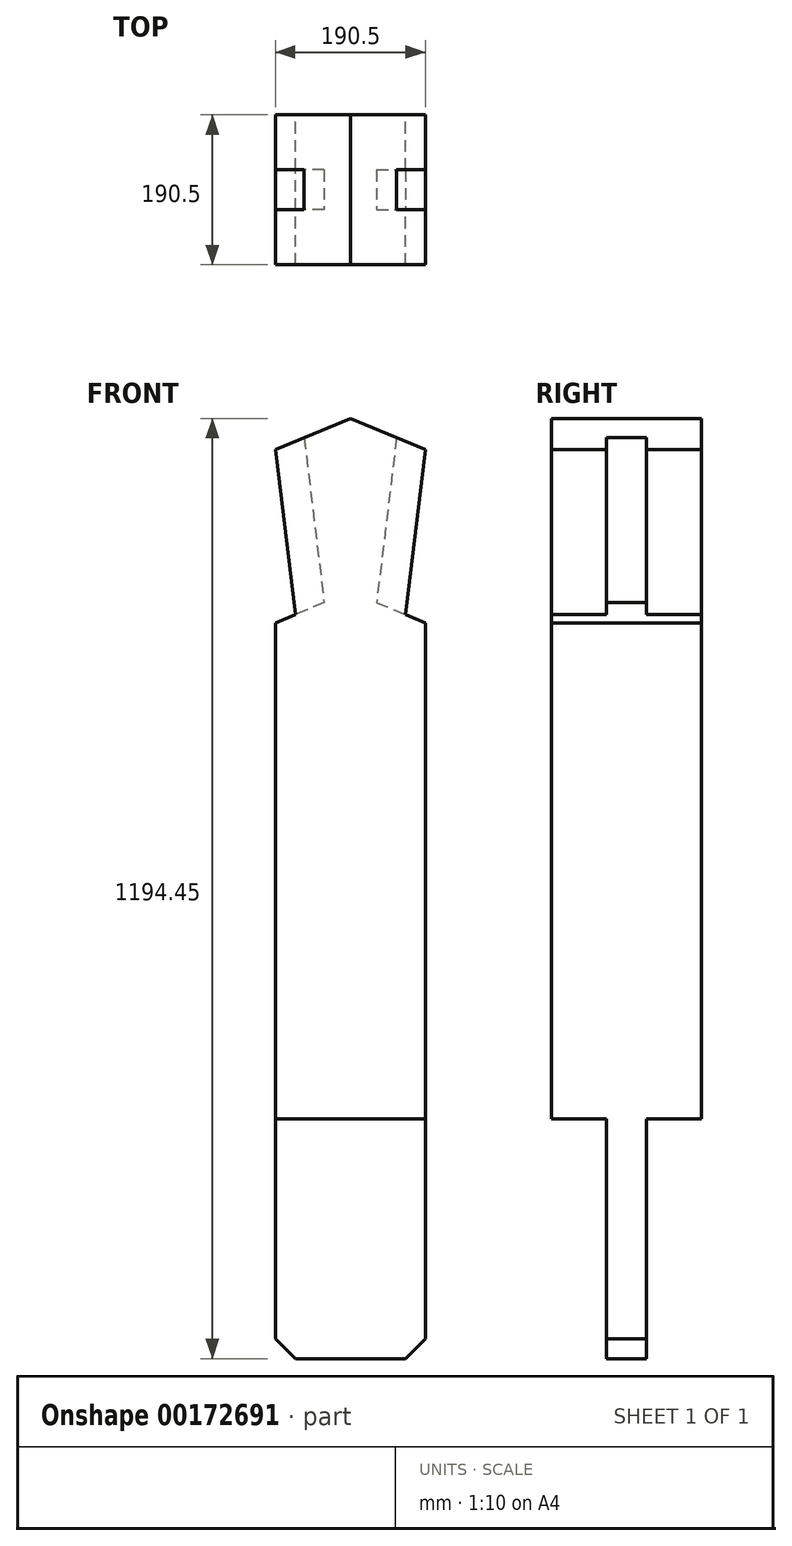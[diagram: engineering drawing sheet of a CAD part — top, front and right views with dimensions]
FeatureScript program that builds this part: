
annotation { "Feature Type Name" : "Feature", "Feature Type Description" : "" }
export const myFeature = defineFeature(function(context is Context, id is Id, definition is map)
    precondition{}
    {
        {
            var Q0;
            Q0=qCreatedBy(makeId("Front.planeOp"),FACE);
            var sketch = newSketch(context, id + "F0", { "sketchPlane" : qUnion([Q0])});
            skLineSegment(sketch, "E0.bottom", {"start": v(-95.25, 1092.85) * mm, "end": v(95.25, 1092.85) * mm});
            skLineSegment(sketch, "E0.top", {"start": v(-95.25, -101.6) * mm, "end": v(95.25, -101.6) * mm});
            skLineSegment(sketch, "E0.left", {"start": v(-95.25, 833.03) * mm, "end": v(-95.25, 203.2) * mm});
            skLineSegment(sketch, "E0.right", {"start": v(95.25, 833.03) * mm, "end": v(95.25, 203.2) * mm});
            skLineSegment(sketch, "E1", {"start": v(-95.25, 0) * mm, "end": v(95.25, 0) * mm});
            skLineSegment(sketch, "E2", {"start": v(95.25, 0) * mm, "end": v(2094.52, 0) * mm});
            skLineSegment(sketch, "E3", {"start": v(2094.52, 0) * mm, "end": v(1606.84, 203.2) * mm});
            skLineSegment(sketch, "E4", {"start": v(1606.84, 203.2) * mm, "end": v(95.25, 203.2) * mm});
            skLineSegment(sketch, "E5", {"start": v(95.25, 203.2) * mm, "end": v(-95.25, 203.2) * mm});
            skLineSegment(sketch, "E6", {"start": v(-95.25, 203.2) * mm, "end": v(-1606.84, 203.2) * mm});
            skLineSegment(sketch, "E7", {"start": v(-1606.84, 203.2) * mm, "end": v(-2094.52, 0) * mm});
            skLineSegment(sketch, "E8", {"start": v(-2094.52, 0) * mm, "end": v(-95.25, 0) * mm});
            skLineSegment(sketch, "E9", {"start": v(1850.68, 101.6) * mm, "end": v(1820.2, 101.6) * mm});
            skLineSegment(sketch, "E10", {"start": v(1820.2, 101.6) * mm, "end": v(1820.2, 114.3) * mm});
            skLineSegment(sketch, "E11", {"start": v(1606.84, 203.2) * mm, "end": v(95.25, 833.03) * mm});
            skLineSegment(sketch, "E12", {"start": v(33.32, 858.84) * mm, "end": v(0, 872.72) * mm});
            skLineSegment(sketch, "E13", {"start": v(0, 872.72) * mm, "end": v(0, 1092.85) * mm});
            skLineSegment(sketch, "E14", {"start": v(0, 1092.85) * mm, "end": v(69.85, 1063.75) * mm});
            skLineSegment(sketch, "E15", {"start": v(95.25, 1053.16) * mm, "end": v(3048, -177.15) * mm});
            skLineSegment(sketch, "E16", {"start": v(3048, -177.15) * mm, "end": v(3048, -397.28) * mm});
            skLineSegment(sketch, "E17", {"start": v(3048, -397.28) * mm, "end": v(2094.52, 0) * mm});
            skLineSegment(sketch, "E18", {"start": v(1014.13, 450.16) * mm, "end": v(1092.29, 637.73) * mm});
            skLineSegment(sketch, "E19", {"start": v(2235.2, -58.62) * mm, "end": v(2235.2, -2361.55) * mm});
            skLineSegment(sketch, "E20", {"start": v(2235.2, -2361.55) * mm, "end": v(2438.4, -2361.55) * mm});
            skLineSegment(sketch, "E21", {"start": v(2438.4, -2361.55) * mm, "end": v(2438.4, -143.28) * mm});
            skLineSegment(sketch, "E22", {"start": v(0, 0) * mm, "end": v(0, -1827.58) * mm});
            skLineSegment(sketch, "E23", {"start": v(2438.4, -143.28) * mm, "end": v(2438.4, 76.85) * mm});
            skLineSegment(sketch, "E24", {"start": v(69.85, 1063.75) * mm, "end": v(69.85, 843.61) * mm});
            skLineSegment(sketch, "E25", {"start": v(95.25, 1053.16) * mm, "end": v(69.85, 843.61) * mm});
            skLineSegment(sketch, "E26.0", {"start": v(58.72, 1068.39) * mm, "end": v(33.32, 858.84) * mm});
            skLineSegment(sketch, "E27.MirrorCS", {"start": v(0, 1092.85) * mm, "end": v(-69.85, 1063.75) * mm});
            skLineSegment(sketch, "E28.MirrorCS", {"start": v(-33.32, 858.84) * mm, "end": v(0, 872.72) * mm});
            skLineSegment(sketch, "E29.MirrorCS", {"start": v(-95.25, 1053.16) * mm, "end": v(-69.85, 843.61) * mm});
            skLineSegment(sketch, "E30.MirrorCS", {"start": v(-1014.13, 450.16) * mm, "end": v(-1092.29, 637.73) * mm});
            skLineSegment(sketch, "E31.MirrorCS", {"start": v(-69.85, 1063.75) * mm, "end": v(-69.85, 843.61) * mm});
            skLineSegment(sketch, "E32.MirrorCS", {"start": v(-58.72, 1068.39) * mm, "end": v(-33.32, 858.84) * mm});
            skLineSegment(sketch, "E33.MirrorCS", {"start": v(-95.25, 1053.16) * mm, "end": v(-3048, -177.15) * mm});
            skLineSegment(sketch, "E34.MirrorCS", {"start": v(-1606.84, 203.2) * mm, "end": v(-95.25, 833.03) * mm});
            skLineSegment(sketch, "E35.MirrorCS", {"start": v(-3048, -177.15) * mm, "end": v(-3048, -397.28) * mm});
            skLineSegment(sketch, "E36.MirrorCS", {"start": v(-3048, -397.28) * mm, "end": v(-2094.52, 0) * mm});
            skLineSegment(sketch, "E37.MirrorCS", {"start": v(-2235.2, -58.62) * mm, "end": v(-2235.2, -2361.55) * mm});
            skLineSegment(sketch, "E38.MirrorCS", {"start": v(-2235.2, -2361.55) * mm, "end": v(-2438.4, -2361.55) * mm});
            skLineSegment(sketch, "E39.MirrorCS", {"start": v(-2438.4, -2361.55) * mm, "end": v(-2438.4, -143.28) * mm});
            skLineSegment(sketch, "E40", {"start": v(95.25, 833.03) * mm, "end": v(95.25, 1053.16) * mm});
            skLineSegment(sketch, "E41", {"start": v(95.25, 1092.85) * mm, "end": v(95.25, 1053.16) * mm});
            skLineSegment(sketch, "E42", {"start": v(-95.25, 833.03) * mm, "end": v(-95.25, 1053.16) * mm});
            skLineSegment(sketch, "E43", {"start": v(-95.25, 1092.85) * mm, "end": v(-95.25, 1053.16) * mm});
            skLineSegment(sketch, "E44", {"start": v(33.32, 858.84) * mm, "end": v(69.85, 843.61) * mm});
            skLineSegment(sketch, "E45", {"start": v(95.25, 833.03) * mm, "end": v(69.85, 843.61) * mm});
            skLineSegment(sketch, "E46", {"start": v(-33.32, 858.84) * mm, "end": v(-69.85, 843.61) * mm});
            skLineSegment(sketch, "E47", {"start": v(-95.25, 833.03) * mm, "end": v(-69.85, 843.61) * mm});
            skLineSegment(sketch, "E48", {"start": v(-95.25, 1053.16) * mm, "end": v(-58.72, 1068.39) * mm});
            skLineSegment(sketch, "E49", {"start": v(58.72, 1068.39) * mm, "end": v(69.85, 1063.75) * mm});
            skLineSegment(sketch, "E50", {"start": v(58.72, 1068.39) * mm, "end": v(95.25, 1053.16) * mm});
            skLineSegment(sketch, "E51", {"start": v(-69.85, 1063.75) * mm, "end": v(-58.72, 1068.39) * mm});
            skLineSegment(sketch, "E52", {"start": v(-95.25, 203.2) * mm, "end": v(-95.25, 0) * mm});
            skLineSegment(sketch, "E53", {"start": v(-95.25, 0) * mm, "end": v(-95.25, -101.6) * mm});
            skLineSegment(sketch, "E54", {"start": v(95.25, 203.2) * mm, "end": v(95.25, 0) * mm});
            skLineSegment(sketch, "E55", {"start": v(95.25, 0) * mm, "end": v(95.25, -101.6) * mm});
            skSolve(sketch);
        }
        {
            var Q0;
            {var subQ0=sQuery(id+"F0.wireOp",EDGE,"E55");Q0=makeQuery(id+"F0.imprint","IMPRINT",FACE,{"disambiguationData":[TD([[makeQuery(id+"F0.imprint","IMPRINT",EDGE,{"derivedFrom":subQ0}),-1.0]])]});}
            var Q1;
            {var subQ0=sQuery(id+"F0.wireOp",EDGE,"E53");Q1=makeQuery(id+"F0.imprint","IMPRINT",FACE,{"disambiguationData":[TD([[makeQuery(id+"F0.imprint","IMPRINT",EDGE,{"derivedFrom":subQ0}),1.0]])]});}
            var Q2;
            Q2=makeQuery(id+"F0.imprint","IMPRINT",FACE,{"disambiguationData":[TD([[makeQuery(id+"F0.imprint","IMPRINT",EDGE,{"derivedFrom":sQuery(id+"F0.wireOp",EDGE,"E5")}),1.0]])]});
            var Q3;
            Q3=makeQuery(id+"F0.imprint","IMPRINT",FACE,{"disambiguationData":[TD([[makeQuery(id+"F0.imprint","IMPRINT",EDGE,{"derivedFrom":sQuery(id+"F0.wireOp",EDGE,"E0.left")}),1.0]])]});
            var Q4;
            Q4=makeQuery(id+"F0.imprint","IMPRINT",FACE,{"disambiguationData":[TD([[makeQuery(id+"F0.imprint","IMPRINT",EDGE,{"derivedFrom":sQuery(id+"F0.wireOp",EDGE,"E13")}),1.0]])]});
            var Q5;
            {var subQ4=sQuery(id+"F0.wireOp",EDGE,"E12");Q5=makeQuery(id+"F0.imprint","IMPRINT",FACE,{"disambiguationData":[TD([[makeQuery(id+"F0.imprint","IMPRINT",EDGE,{"derivedFrom":subQ4}),-1.0]])]});}
            var Q6;
            {var subQ0=sQuery(id+"F0.wireOp",EDGE,"E51");Q6=makeQuery(id+"F0.imprint","IMPRINT",FACE,{"disambiguationData":[TD([[makeQuery(id+"F0.imprint","IMPRINT",EDGE,{"derivedFrom":subQ0}),-1.0]])]});}
            var Q7;
            {var subQ0=sQuery(id+"F0.wireOp",EDGE,"E49");Q7=makeQuery(id+"F0.imprint","IMPRINT",FACE,{"disambiguationData":[TD([[makeQuery(id+"F0.imprint","IMPRINT",EDGE,{"derivedFrom":subQ0}),-1.0]])]});}
            var Q8;
            {var subQ0=sQuery(id+"F0.wireOp",EDGE,"E46");Q8=makeQuery(id+"F0.imprint","IMPRINT",FACE,{"disambiguationData":[TD([[makeQuery(id+"F0.imprint","IMPRINT",EDGE,{"derivedFrom":subQ0}),-1.0]])]});}
            var Q9;
            {var subQ0=sQuery(id+"F0.wireOp",EDGE,"E29.MirrorCS");Q9=makeQuery(id+"F0.imprint","IMPRINT",FACE,{"disambiguationData":[TD([[makeQuery(id+"F0.imprint","IMPRINT",EDGE,{"derivedFrom":subQ0}),1.0]])]});}
            var Q10;
            {var subQ0=sQuery(id+"F0.wireOp",EDGE,"E25");Q10=makeQuery(id+"F0.imprint","IMPRINT",FACE,{"disambiguationData":[TD([[makeQuery(id+"F0.imprint","IMPRINT",EDGE,{"derivedFrom":subQ0}),-1.0]])]});}
            var Q11;
            {var subQ0=sQuery(id+"F0.wireOp",EDGE,"E44");Q11=makeQuery(id+"F0.imprint","IMPRINT",FACE,{"disambiguationData":[TD([[makeQuery(id+"F0.imprint","IMPRINT",EDGE,{"derivedFrom":subQ0}),1.0]])]});}
            extrude(context, id + "F1", {"entities" : qUnion([Q0, Q1, Q2, Q3, Q4, Q5, Q6, Q7, Q8, Q9, Q10, Q11]), "endBound" : BoundingType.SYMMETRIC, "depth" : 190.5 * mm});
        }
        {
            var Q0;
            Q0=qCreatedBy(makeId("Right.planeOp"),FACE);
            var sketch = newSketch(context, id + "F2", { "sketchPlane" : qUnion([Q0])});
            skLineSegment(sketch, "E56.bottom", {"start": v(-95.25, -101.6) * mm, "end": v(-25.4, -101.6) * mm});
            skLineSegment(sketch, "E56.top", {"start": v(-95.25, 203.2) * mm, "end": v(-25.4, 203.2) * mm});
            skLineSegment(sketch, "E56.left", {"start": v(-95.25, -101.6) * mm, "end": v(-95.25, 203.2) * mm});
            skLineSegment(sketch, "E56.right", {"start": v(-25.4, -101.6) * mm, "end": v(-25.4, 203.2) * mm});
            skLineSegment(sketch, "E57.bottom", {"start": v(95.25, -101.6) * mm, "end": v(25.4, -101.6) * mm});
            skLineSegment(sketch, "E57.top", {"start": v(95.25, 203.2) * mm, "end": v(25.4, 203.2) * mm});
            skLineSegment(sketch, "E57.left", {"start": v(95.25, -101.6) * mm, "end": v(95.25, 203.2) * mm});
            skLineSegment(sketch, "E57.right", {"start": v(25.4, -101.6) * mm, "end": v(25.4, 203.2) * mm});
            skSolve(sketch);
        }
        {
            var Q0;
            Q0 = qSketchRegion(id + "F2", true);
            extrude(context, id + "F3", {"entities" : qUnion([Q0]), "operationType" : NewBodyOperationType.REMOVE, "endBound" : BoundingType.THROUGH_ALL, "oppositeDirection" : true, "depth" : 25.4 * mm, "hasSecondDirection" : true, "secondDirectionBound" : SecondDirectionBoundingType.THROUGH_ALL, "secondDirectionOppositeDirection" : false, "secondDirectionDepth" : 25.4 * mm});
        }
        {
            var Q0;
            Q0=makeQuery(id+"F1.opExtrude","SWEPT_FACE",FACE,{"disambiguationData":[OSD([sQuery(id+"F0.wireOp",EDGE,"E14"),sQuery(id+"F0.wireOp",EDGE,"E49"),sQuery(id+"F0.wireOp",EDGE,"E50")])]});
            var sketch = newSketch(context, id + "F4", { "sketchPlane" : qUnion([Q0])});
            skLineSegment(sketch, "E58.bottom", {"start": v(-356.72, 25.4) * mm, "end": v(-317.14, 25.4) * mm});
            skLineSegment(sketch, "E58.top", {"start": v(-356.72, -25.4) * mm, "end": v(-317.14, -25.4) * mm});
            skLineSegment(sketch, "E58.left", {"start": v(-356.72, 25.4) * mm, "end": v(-356.72, -25.4) * mm});
            skLineSegment(sketch, "E58.right", {"start": v(-317.14, 25.4) * mm, "end": v(-317.14, -25.4) * mm});
            skSolve(sketch);
        }
        {
            var Q0;
            Q0=makeQuery(id+"F1.opExtrude","SWEPT_EDGE",EDGE,{"disambiguationData":[OSD([sQuery(id+"F0.wireOp",EDGE,"E0.top"),sQuery(id+"F0.wireOp",EDGE,"E55")])]});
            chamfer(context, id + "F5", {"entities" : qUnion([Q0]), "width" : 25.4 * mm, "tangentPropagation" : true});
        }
        {
            var Q0;
            Q0=makeQuery(id+"F1.opExtrude","SWEPT_EDGE",EDGE,{"disambiguationData":[OSD([sQuery(id+"F0.wireOp",EDGE,"E0.top"),sQuery(id+"F0.wireOp",EDGE,"E53")])]});
            chamfer(context, id + "F6", {"entities" : qUnion([Q0]), "width" : 25.4 * mm, "tangentPropagation" : true});
        }
        {
            var Q0;
            Q0=qCreatedBy(makeId("Front.planeOp"),FACE);
            var sketch = newSketch(context, id + "F7", { "sketchPlane" : qUnion([Q0])});
            skLineSegment(sketch, "E59", {"start": v(33.32, 858.84) * mm, "end": v(69.85, 843.61) * mm});
            skLineSegment(sketch, "E60", {"start": v(69.85, 843.61) * mm, "end": v(95.25, 1053.16) * mm});
            skLineSegment(sketch, "E61", {"start": v(95.25, 1053.16) * mm, "end": v(58.72, 1068.39) * mm});
            skLineSegment(sketch, "E62", {"start": v(58.72, 1068.39) * mm, "end": v(33.32, 858.84) * mm});
            skLineSegment(sketch, "E63", {"start": v(-58.72, 1068.39) * mm, "end": v(-33.32, 858.84) * mm});
            skLineSegment(sketch, "E64", {"start": v(-33.32, 858.84) * mm, "end": v(-69.85, 843.61) * mm});
            skLineSegment(sketch, "E65", {"start": v(-69.85, 843.61) * mm, "end": v(-95.25, 1053.16) * mm});
            skLineSegment(sketch, "E66", {"start": v(-95.25, 1053.16) * mm, "end": v(-58.72, 1068.39) * mm});
            skSolve(sketch);
        }
        {
            var Q0;
            Q0 = qSketchRegion(id + "F7", true);
            extrude(context, id + "F8", {"entities" : qUnion([Q0]), "operationType" : NewBodyOperationType.REMOVE, "endBound" : BoundingType.SYMMETRIC, "oppositeDirection" : true, "depth" : 50.8 * mm});
        }
    });
